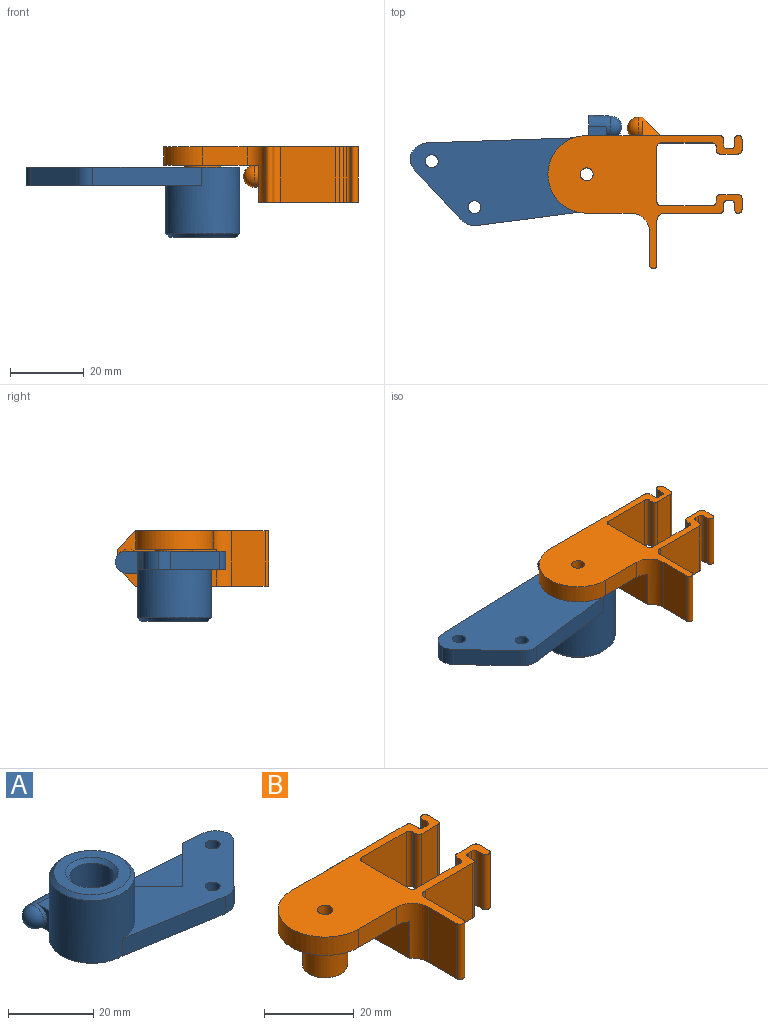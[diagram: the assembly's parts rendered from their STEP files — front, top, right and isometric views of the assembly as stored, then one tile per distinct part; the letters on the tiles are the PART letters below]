
ASSEMBLY  parts=2 mates=1
PART A: 24 faces, bbox 57.9x31x19 mm
  f0: plane 47.91x24.9mm, normal (0,0,1), area 558.5mm2, adj f1,f2,f3,f4,f5,f6,f8,f9
  f1: plane 43.4x18mm, normal (0.07,1,0), area 155.5mm2, adj f0,f2,f10,f11,f13,f18,f19,f20
  f2: cylinder r=10mm len=20mm, axis (0,0,-1), area 924.2mm2, adj f0,f1,f3,f11,f14,f15,f21
  f3: plane 29.17x5mm, normal (-0.17,-0.99,0), area 147.9mm2, adj f0,f2,f4,f11
  f4: cylinder r=5mm len=5mm, axis (0,0,-1), area 23.8mm2, adj f0,f3,f5,f11
  f5: plane 12.93x12.93mm, normal (0.71,-0.71,0), area 91.5mm2, adj f0,f4,f6,f11
  f6: cylinder r=5mm len=5mm, axis (0,0,-1), area 17.1mm2, adj f0,f5,f10,f11
  f7: cylinder r=5.2mm len=18mm, axis (0,0,-1), area 588.1mm2, adj f11,f23
  f8: cylinder r=1.75mm len=5mm, axis (0,0,-1), area 55mm2, adj f0,f11
  f9: cylinder r=1.75mm len=5mm, axis (0,0,-1), area 55mm2, adj f0,f11
  f10: cylinder r=4.87mm len=5mm, axis (0,0,-1), area 34.8mm2, adj f0,f1,f6,f11
  f11: plane 57.91x28mm, normal (0,0,-1), area 982.1mm2, adj f1,f2,f3,f4,f5,f6,f7,f8
  f12: plane 18x18mm, normal (0,0,1), area 133.7mm2, adj f21,f22,f23
  f13: plane 6x6mm, normal (1,0,0), area 32.1mm2, adj f1,f11,f15,f16
  f14: plane 6x4.34mm, normal (-1,0,0), area 11.9mm2, adj f2,f11,f15,f16
  f15: plane 5x4.34mm, normal (0,0,1), area 17.2mm2, adj f2,f13,f14,f16
  f16: cylinder r=3mm len=6mm, axis (-1,0,0), area 66mm2, adj f11,f13,f14,f15,f17
  f17: sphere r=3mm, area 56.5mm2, adj f16
  f18: plane 14.29x14.29mm, normal (0.71,0.71,0), area 60.6mm2, adj f0,f1,f19,f20
  f19: plane 12.41x12.41mm, normal (-0.71,0.71,0), area 52.6mm2, adj f0,f1,f18,f20
  f20: plane 26.7x14.29mm, normal (0,0,1), area 177.3mm2, adj f1,f18,f19
  f21: cone r=9mm half-angle=45deg, axis (0,0,-1), area 82.5mm2, adj f2,f12,f22
  f22: plane 1.44x1.1mm, normal (0.05,0.71,0.71), area 1.9mm2, adj f1,f12,f21
  f23: cone r=5.2mm half-angle=45deg, axis (0,0,1), area 50.6mm2, adj f7,f12
PART B: 55 faces, bbox 52.5x41x15 mm
  f0: plane 15x15mm, normal (0,-1,0), area 225mm2, adj f21,f27,f33,f51
  f1: plane 15x5mm, normal (0,1,0), area 75mm2, adj f16,f21,f22,f23
  f2: plane 16x15mm, normal (0,1,0), area 240mm2, adj f21,f27,f32,f46
  f3: plane 12x5mm, normal (0,-1,0), area 60mm2, adj f21,f22,f23,f53
  f4: plane 15x3mm, normal (1,0,0), area 45mm2, adj f21,f27,f29,f42
  f5: plane 15x5mm, normal (0,1,0), area 75mm2, adj f21,f27,f35,f42
  f6: plane 15x1mm, normal (-1,0,0), area 15mm2, adj f21,f27,f35,f36
  f7: plane 15x14mm, normal (0,1,0), area 210mm2, adj f21,f27,f36,f37
  f8: plane 15x15mm, normal (1,0,0), area 225mm2, adj f21,f27,f37,f38
  f9: plane 15x14mm, normal (0,-1,0), area 210mm2, adj f21,f27,f38,f39
  f10: plane 15x1mm, normal (-1,0,0), area 15mm2, adj f21,f27,f39,f40
  f11: plane 15x5mm, normal (0,-1,0), area 75mm2, adj f21,f27,f40,f43
  f12: plane 15x3mm, normal (1,0,0), area 45mm2, adj f21,f27,f31,f43
  f13: plane 15x1.6mm, normal (-1,0,0), area 24mm2, adj f21,f27,f30,f31
  f14: plane 15x1mm, normal (0,1,0), area 15mm2, adj f21,f27,f30,f41
  f15: plane 15x1.6mm, normal (1,0,0), area 24mm2, adj f21,f27,f32,f41
  f16: plane 27x15mm, normal (-1,0,0), area 241.7mm2, adj f1,f22,f27,f44,f45,f46,f47,f53
  f17: plane 15x1.43mm, normal (1,0,0), area 21.5mm2, adj f21,f27,f33,f34
  f18: plane 15x1mm, normal (0,-1,0), area 15mm2, adj f21,f27,f28,f34
  f19: plane 15x1.43mm, normal (-1,0,0), area 21.5mm2, adj f21,f27,f28,f29
  f20: cylinder r=5mm len=10mm, axis (0,0,1), area 307.9mm2, adj f25,f26
  f21: plane 52.5x36mm, normal (0,0,1), area 710.8mm2, adj f0,f1,f2,f3,f4,f5,f6,f7
  f22: plane 25.5x22mm, normal (0,0,-1), area 312.4mm2, adj f1,f3,f16,f23,f24,f53
  f23: cylinder r=10.5mm len=21mm, axis (0,0,1), area 164.9mm2, adj f1,f3,f21,f22
  f24: cylinder r=7.5mm len=15mm, axis (0,0,1), area 9.4mm2, adj f22,f25
  f25: plane 15x15mm, normal (0,0,-1), area 98.2mm2, adj f20,f24
  f26: plane 10x10mm, normal (0,0,-1), area 68.9mm2, adj f20,f52
  f27: plane 36x27mm, normal (0,0,-1), area 231.3mm2, adj f0,f2,f4,f5,f6,f7,f8,f9
  f28: cylinder r=1mm len=15mm, axis (0,0,1), area 23.6mm2, adj f18,f19,f21,f27
  f29: cylinder r=1mm len=15mm, axis (0,0,-1), area 47.1mm2, adj f4,f19,f21,f27
  f30: cylinder r=1mm len=15mm, axis (0,0,1), area 23.6mm2, adj f13,f14,f21,f27
  f31: cylinder r=1mm len=15mm, axis (0,0,1), area 47.1mm2, adj f12,f13,f21,f27
  f32: cylinder r=1mm len=15mm, axis (0,0,-1), area 23.6mm2, adj f2,f15,f21,f27
  f33: cylinder r=1mm len=15mm, axis (0,0,-1), area 23.6mm2, adj f0,f17,f21,f27
  f34: cylinder r=1mm len=15mm, axis (0,0,1), area 23.6mm2, adj f17,f18,f21,f27
  f35: cylinder r=1mm len=15mm, axis (0,0,1), area 23.6mm2, adj f5,f6,f21,f27
  f36: cylinder r=1mm len=15mm, axis (0,0,-1), area 23.6mm2, adj f6,f7,f21,f27
  f37: cylinder r=1mm len=15mm, axis (0,0,-1), area 23.6mm2, adj f7,f8,f21,f27
  f38: cylinder r=1mm len=15mm, axis (0,0,1), area 23.6mm2, adj f8,f9,f21,f27
  f39: cylinder r=1mm len=15mm, axis (0,0,-1), area 23.6mm2, adj f9,f10,f21,f27
  f40: cylinder r=1mm len=15mm, axis (0,0,1), area 23.6mm2, adj f10,f11,f21,f27
  f41: cylinder r=1mm len=15mm, axis (0,0,1), area 23.6mm2, adj f14,f15,f21,f27
  f42: cylinder r=1mm len=15mm, axis (0,0,1), area 23.6mm2, adj f4,f5,f21,f27
  f43: cylinder r=1mm len=15mm, axis (0,0,1), area 23.6mm2, adj f11,f12,f21,f27
  f44: plane 5x5mm, normal (0,0.71,0.71), area 17.7mm2, adj f16,f21,f46
  f45: plane 5x5mm, normal (0,0.71,-0.71), area 17.7mm2, adj f16,f27,f46
  f46: plane 15x5mm, normal (0.71,0.71,0), area 70.7mm2, adj f2,f16,f44,f45
  f47: cylinder r=3mm len=6mm, axis (1,0,0), area 18.8mm2, adj f16,f48
  f48: sphere r=3mm, area 56.5mm2, adj f47
  f49: plane 15x9mm, normal (-1,0,0), area 135mm2, adj f21,f27,f53,f54
  f50: plane 15x12mm, normal (1,0,0), area 180mm2, adj f21,f27,f51,f54
  f51: cylinder r=2mm len=15mm, axis (0,0,-1), area 47.1mm2, adj f0,f21,f27,f50
  f52: cylinder r=1.75mm len=15mm, axis (0,0,1), area 164.9mm2, adj f21,f26
  f53: cylinder r=5mm len=15mm, axis (0,0,1), area 85.6mm2, adj f3,f16,f21,f22,f27,f49
  f54: cylinder r=1mm len=15mm, axis (0,0,1), area 47.1mm2, adj f21,f27,f49,f50
PLACE A rot(axis=(-0.02,-1,0),180deg) t=(13.54,52.33,15.81)mm
PLACE B t=(28.17,31.84,-3.71)mm
MATE cylindrical A.f7 <-> B.f20  axis (0,0,1) through (13.17,42.34,15.81)mm
